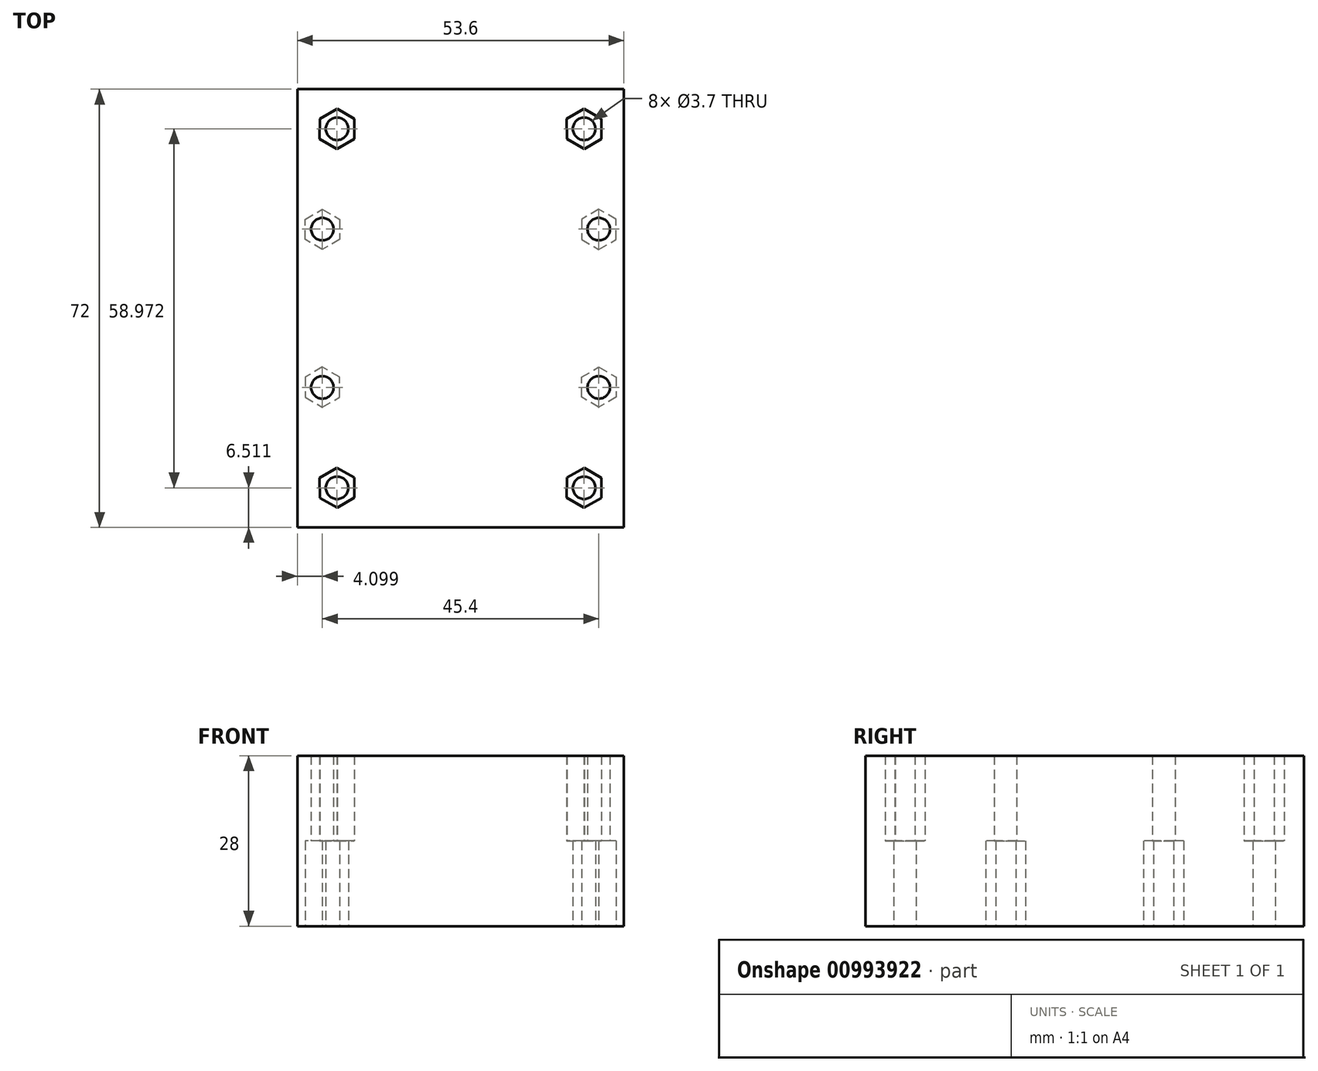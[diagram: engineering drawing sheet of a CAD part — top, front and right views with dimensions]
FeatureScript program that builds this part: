
annotation { "Feature Type Name" : "Feature", "Feature Type Description" : "" }
export const myFeature = defineFeature(function(context is Context, id is Id, definition is map)
    precondition{}
    {
        {
            var Q0;
            Q0=qCreatedBy(makeId("Top.planeOp"),FACE);
            var sketch = newSketch(context, id + "F0", { "sketchPlane" : qUnion([Q0])});
            skLineSegment(sketch, "E0.bottom", {"start": v(27.07, 35.85) * mm, "end": v(-26.53, 35.85) * mm});
            skLineSegment(sketch, "E0.top", {"start": v(27.07, -36.15) * mm, "end": v(-26.53, -36.15) * mm});
            skLineSegment(sketch, "E0.left", {"start": v(27.07, 35.85) * mm, "end": v(27.07, -36.15) * mm});
            skLineSegment(sketch, "E0.right", {"start": v(-26.53, 35.85) * mm, "end": v(-26.53, -36.15) * mm});
            skPoint(sketch, "E0.middle", {"position": v(0.27, -0.15) * mm});
            skCircle(sketch, "E1.cCircle", {"center": v(-22.43, 12.8) * mm, "radius": 2.85 * mm, "construction": true});
            skLineSegment(sketch, "E1.0", {"start": v(-19.58, 14.45) * mm, "end": v(-19.58, 11.16) * mm});
            skLineSegment(sketch, "E1.1", {"start": v(-19.58, 11.16) * mm, "end": v(-22.43, 9.52) * mm});
            skLineSegment(sketch, "E1.2", {"start": v(-22.43, 9.52) * mm, "end": v(-25.28, 11.16) * mm});
            skLineSegment(sketch, "E1.3", {"start": v(-25.28, 11.16) * mm, "end": v(-25.28, 14.45) * mm});
            skLineSegment(sketch, "E1.4", {"start": v(-25.28, 14.45) * mm, "end": v(-22.43, 16.1) * mm});
            skLineSegment(sketch, "E1.5", {"start": v(-22.43, 16.1) * mm, "end": v(-19.58, 14.45) * mm});
            skPoint(sketch, "E1.0.midPoint", {"position": v(-19.58, 12.8) * mm});
            skLineSegment(sketch, "E2", {"start": v(-25.28, 14.45) * mm, "end": v(-26.53, 14.45) * mm, "construction": true});
            skLineSegment(sketch, "E3", {"start": v(-26.53, -0.15) * mm, "end": v(27.07, -0.15) * mm, "construction": true});
            skLineSegment(sketch, "E4", {"start": v(0.27, 35.85) * mm, "end": v(0.27, -36.15) * mm, "construction": true});
            skLineSegment(sketch, "E5.MirrorCS", {"start": v(-22.43, -16.4) * mm, "end": v(-19.58, -14.76) * mm});
            skCircle(sketch, "E6.MirrorC", {"center": v(-22.43, -13.11) * mm, "radius": 2.85 * mm, "construction": true});
            skLineSegment(sketch, "E7.MirrorCS", {"start": v(-25.28, -14.76) * mm, "end": v(-22.43, -16.4) * mm});
            skLineSegment(sketch, "E8.MirrorCS", {"start": v(-25.28, -11.47) * mm, "end": v(-25.28, -14.76) * mm});
            skLineSegment(sketch, "E9.MirrorCS", {"start": v(-22.43, -9.82) * mm, "end": v(-25.28, -11.47) * mm});
            skPoint(sketch, "E10.MirrorP", {"position": v(-19.58, -13.11) * mm});
            skLineSegment(sketch, "E11.MirrorCS", {"start": v(-19.58, -14.76) * mm, "end": v(-19.58, -11.47) * mm});
            skLineSegment(sketch, "E12.MirrorCS", {"start": v(-19.58, -11.47) * mm, "end": v(-22.43, -9.82) * mm});
            skLineSegment(sketch, "E13.MirrorCS", {"start": v(25.82, -11.47) * mm, "end": v(25.82, -14.76) * mm});
            skLineSegment(sketch, "E14.MirrorCS", {"start": v(22.97, 9.52) * mm, "end": v(25.82, 11.16) * mm});
            skLineSegment(sketch, "E15.MirrorCS", {"start": v(22.97, -16.4) * mm, "end": v(20.12, -14.76) * mm});
            skLineSegment(sketch, "E16.MirrorCS", {"start": v(22.97, 16.1) * mm, "end": v(20.12, 14.45) * mm});
            skLineSegment(sketch, "E17.MirrorCS", {"start": v(20.12, -11.47) * mm, "end": v(22.97, -9.82) * mm});
            skLineSegment(sketch, "E18.MirrorCS", {"start": v(20.12, -14.76) * mm, "end": v(20.12, -11.47) * mm});
            skLineSegment(sketch, "E19.MirrorCS", {"start": v(25.82, 14.45) * mm, "end": v(22.97, 16.1) * mm});
            skLineSegment(sketch, "E20.MirrorCS", {"start": v(25.82, -14.76) * mm, "end": v(22.97, -16.4) * mm});
            skLineSegment(sketch, "E21.MirrorCS", {"start": v(20.12, 14.45) * mm, "end": v(20.12, 11.16) * mm});
            skCircle(sketch, "E22.MirrorC", {"center": v(22.97, 12.8) * mm, "radius": 2.85 * mm, "construction": true});
            skLineSegment(sketch, "E23.MirrorCS", {"start": v(20.12, 11.16) * mm, "end": v(22.97, 9.52) * mm});
            skLineSegment(sketch, "E24.MirrorCS", {"start": v(25.82, 11.16) * mm, "end": v(25.82, 14.45) * mm});
            skLineSegment(sketch, "E25.MirrorCS", {"start": v(22.97, -9.82) * mm, "end": v(25.82, -11.47) * mm});
            skCircle(sketch, "E26.MirrorC", {"center": v(22.97, -13.11) * mm, "radius": 2.85 * mm, "construction": true});
            skPoint(sketch, "E27.MirrorP", {"position": v(20.12, -13.11) * mm});
            skPoint(sketch, "E28.MirrorP", {"position": v(20.12, 12.8) * mm});
            skCircle(sketch, "E29.MirrorC", {"center": v(-20.01, 29.33) * mm, "radius": 1.85 * mm});
            skCircle(sketch, "E30.MirrorC", {"center": v(20.56, 29.33) * mm, "radius": 1.85 * mm});
            skLineSegment(sketch, "E31.MirrorCS", {"start": v(0.27, -36.15) * mm, "end": v(0.27, 35.85) * mm, "construction": true});
            skCircle(sketch, "E32.MirrorC", {"center": v(-20.01, -29.64) * mm, "radius": 1.85 * mm});
            skCircle(sketch, "E33.MirrorC", {"center": v(20.56, -29.64) * mm, "radius": 1.85 * mm});
            skSolve(sketch);
        }
        {
            var Q0;
            Q0=qSketchRegion(id+"F0",true);
            extrude(context, id + "F1", {"entities" : qUnion([Q0]), "depth" : 14 * mm});
        }
        {
            var Q0;
            Q0=makeQuery(id+"F1.opExtrude","CAP_FACE",FACE,{"disambiguationData":[OSD([sQuery(id+"F0.wireOp",EDGE,"E1.0"),sQuery(id+"F0.wireOp",EDGE,"E1.1"),sQuery(id+"F0.wireOp",EDGE,"E1.2"),sQuery(id+"F0.wireOp",EDGE,"E1.3"),sQuery(id+"F0.wireOp",EDGE,"E1.4"),sQuery(id+"F0.wireOp",EDGE,"E1.5"),sQuery(id+"F0.wireOp",EDGE,"E5.MirrorCS"),sQuery(id+"F0.wireOp",EDGE,"E7.MirrorCS"),sQuery(id+"F0.wireOp",EDGE,"E8.MirrorCS"),sQuery(id+"F0.wireOp",EDGE,"E9.MirrorCS"),sQuery(id+"F0.wireOp",EDGE,"E11.MirrorCS"),sQuery(id+"F0.wireOp",EDGE,"E12.MirrorCS"),sQuery(id+"F0.wireOp",EDGE,"E13.MirrorCS"),sQuery(id+"F0.wireOp",EDGE,"E14.MirrorCS"),sQuery(id+"F0.wireOp",EDGE,"E15.MirrorCS"),sQuery(id+"F0.wireOp",EDGE,"E16.MirrorCS"),sQuery(id+"F0.wireOp",EDGE,"E17.MirrorCS"),sQuery(id+"F0.wireOp",EDGE,"E18.MirrorCS"),sQuery(id+"F0.wireOp",EDGE,"E19.MirrorCS"),sQuery(id+"F0.wireOp",EDGE,"E20.MirrorCS"),sQuery(id+"F0.wireOp",EDGE,"E21.MirrorCS"),sQuery(id+"F0.wireOp",EDGE,"E23.MirrorCS"),sQuery(id+"F0.wireOp",EDGE,"E24.MirrorCS"),sQuery(id+"F0.wireOp",EDGE,"E25.MirrorCS"),sQuery(id+"F0.wireOp",EDGE,"E29.MirrorC"),sQuery(id+"F0.wireOp",EDGE,"E30.MirrorC"),sQuery(id+"F0.wireOp",EDGE,"E0.bottom"),sQuery(id+"F0.wireOp",EDGE,"E0.top"),sQuery(id+"F0.wireOp",EDGE,"E0.left"),sQuery(id+"F0.wireOp",EDGE,"E0.right"),sQuery(id+"F0.wireOp",EDGE,"E32.MirrorC"),sQuery(id+"F0.wireOp",EDGE,"E33.MirrorC")])],"isStart":false});
            var sketch = newSketch(context, id + "F2", { "sketchPlane" : qUnion([Q0])});
            skLineSegment(sketch, "E34.bottom", {"start": v(27.07, 35.85) * mm, "end": v(-26.53, 35.85) * mm});
            skLineSegment(sketch, "E34.top", {"start": v(27.07, -36.15) * mm, "end": v(-26.53, -36.15) * mm});
            skLineSegment(sketch, "E34.left", {"start": v(27.07, 35.85) * mm, "end": v(27.07, -36.15) * mm});
            skLineSegment(sketch, "E34.right", {"start": v(-26.53, 35.85) * mm, "end": v(-26.53, -36.15) * mm});
            skPoint(sketch, "E34.middle", {"position": v(0.27, -0.15) * mm});
            skLineSegment(sketch, "E35", {"start": v(-26.53, -0.15) * mm, "end": v(27.07, -0.15) * mm, "construction": true});
            skLineSegment(sketch, "E36", {"start": v(0.27, 35.85) * mm, "end": v(0.27, -36.15) * mm, "construction": true});
            skCircle(sketch, "E37.cCircle", {"center": v(-20.02, 29.34) * mm, "radius": 2.85 * mm, "construction": true});
            skLineSegment(sketch, "E37.0", {"start": v(-17.18, 27.68) * mm, "end": v(-20.03, 26.05) * mm});
            skLineSegment(sketch, "E37.1", {"start": v(-20.03, 26.05) * mm, "end": v(-22.88, 27.7) * mm});
            skLineSegment(sketch, "E37.2", {"start": v(-22.88, 27.7) * mm, "end": v(-22.86, 31) * mm});
            skLineSegment(sketch, "E37.3", {"start": v(-22.86, 31) * mm, "end": v(-20, 32.63) * mm});
            skLineSegment(sketch, "E37.4", {"start": v(-20, 32.63) * mm, "end": v(-17.16, 30.97) * mm});
            skLineSegment(sketch, "E37.5", {"start": v(-17.16, 30.97) * mm, "end": v(-17.18, 27.68) * mm});
            skPoint(sketch, "E37.0.midPoint", {"position": v(-18.6, 26.86) * mm});
            skLineSegment(sketch, "E38.trimOffspring", {"start": v(-22.87, 29.34) * mm, "end": v(-26.53, 29.34) * mm, "construction": true});
            skLineSegment(sketch, "E39.trimOffspring", {"start": v(-20.02, 32.19) * mm, "end": v(-20.02, 35.85) * mm, "construction": true});
            skLineSegment(sketch, "E40.MirrorCS", {"start": v(20.55, 32.19) * mm, "end": v(20.55, 35.85) * mm, "construction": true});
            skLineSegment(sketch, "E41.MirrorCS", {"start": v(17.71, 27.68) * mm, "end": v(20.57, 26.05) * mm});
            skLineSegment(sketch, "E42.MirrorCS", {"start": v(17.7, 30.97) * mm, "end": v(17.71, 27.68) * mm});
            skLineSegment(sketch, "E43.MirrorCS", {"start": v(20.57, 26.05) * mm, "end": v(23.41, 27.7) * mm});
            skLineSegment(sketch, "E44.MirrorCS", {"start": v(23.41, 27.7) * mm, "end": v(23.4, 31) * mm});
            skPoint(sketch, "E45.MirrorP", {"position": v(19.14, 26.86) * mm});
            skCircle(sketch, "E46.MirrorC", {"center": v(20.55, 29.34) * mm, "radius": 2.85 * mm, "construction": true});
            skLineSegment(sketch, "E47.MirrorCS", {"start": v(23.4, 31) * mm, "end": v(20.54, 32.63) * mm});
            skLineSegment(sketch, "E48.MirrorCS", {"start": v(23.4, 29.34) * mm, "end": v(27.07, 29.34) * mm, "construction": true});
            skLineSegment(sketch, "E49.MirrorCS", {"start": v(20.54, 32.63) * mm, "end": v(17.7, 30.97) * mm});
            skCircle(sketch, "E50.MirrorC", {"center": v(22.97, 12.85) * mm, "radius": 1.85 * mm});
            skCircle(sketch, "E51.MirrorC", {"center": v(-22.43, 12.85) * mm, "radius": 1.85 * mm});
            skCircle(sketch, "E52.MirrorC", {"center": v(-22.43, -13.15) * mm, "radius": 1.85 * mm});
            skCircle(sketch, "E53.MirrorC", {"center": v(22.97, -13.15) * mm, "radius": 1.85 * mm});
            skLineSegment(sketch, "E54.MirrorCS", {"start": v(23.4, -31.3) * mm, "end": v(20.54, -32.93) * mm});
            skLineSegment(sketch, "E55.MirrorCS", {"start": v(-20.03, -26.34) * mm, "end": v(-22.88, -28) * mm});
            skLineSegment(sketch, "E56.MirrorCS", {"start": v(-17.18, -27.98) * mm, "end": v(-20.03, -26.34) * mm});
            skLineSegment(sketch, "E57.MirrorCS", {"start": v(20.54, -32.93) * mm, "end": v(17.7, -31.27) * mm});
            skLineSegment(sketch, "E58.MirrorCS", {"start": v(23.41, -28) * mm, "end": v(23.4, -31.3) * mm});
            skLineSegment(sketch, "E59.MirrorCS", {"start": v(-22.86, -31.3) * mm, "end": v(-20, -32.93) * mm});
            skLineSegment(sketch, "E60.MirrorCS", {"start": v(17.71, -27.98) * mm, "end": v(20.57, -26.34) * mm});
            skLineSegment(sketch, "E61.MirrorCS", {"start": v(-20.02, -32.49) * mm, "end": v(-20.02, -36.15) * mm, "construction": true});
            skLineSegment(sketch, "E62.MirrorCS", {"start": v(20.57, -26.34) * mm, "end": v(23.41, -28) * mm});
            skLineSegment(sketch, "E63.MirrorCS", {"start": v(20.55, -32.49) * mm, "end": v(20.55, -36.15) * mm, "construction": true});
            skLineSegment(sketch, "E64.MirrorCS", {"start": v(-20, -32.93) * mm, "end": v(-17.16, -31.27) * mm});
            skLineSegment(sketch, "E65.MirrorCS", {"start": v(0.27, -36.15) * mm, "end": v(0.27, 35.85) * mm, "construction": true});
            skLineSegment(sketch, "E66.MirrorCS", {"start": v(-17.16, -31.27) * mm, "end": v(-17.18, -27.98) * mm});
            skLineSegment(sketch, "E67.MirrorCS", {"start": v(17.7, -31.27) * mm, "end": v(17.71, -27.98) * mm});
            skLineSegment(sketch, "E68.MirrorCS", {"start": v(-22.88, -28) * mm, "end": v(-22.86, -31.3) * mm});
            skLineSegment(sketch, "E69.MirrorCS", {"start": v(23.4, -29.64) * mm, "end": v(27.07, -29.64) * mm, "construction": true});
            skPoint(sketch, "E70.MirrorP", {"position": v(-18.6, -27.16) * mm});
            skCircle(sketch, "E71.MirrorC", {"center": v(20.55, -29.64) * mm, "radius": 2.85 * mm, "construction": true});
            skCircle(sketch, "E72.MirrorC", {"center": v(-20.02, -29.64) * mm, "radius": 2.85 * mm, "construction": true});
            skLineSegment(sketch, "E73.MirrorCS", {"start": v(-22.87, -29.64) * mm, "end": v(-26.53, -29.64) * mm, "construction": true});
            skPoint(sketch, "E74.MirrorP", {"position": v(19.14, -27.16) * mm});
            skSolve(sketch);
        }
        {
            var Q0;
            Q0=qSketchRegion(id+"F2",true);
            extrude(context, id + "F3", {"entities" : qUnion([Q0]), "operationType" : NewBodyOperationType.ADD, "depth" : 14 * mm});
        }
    });
